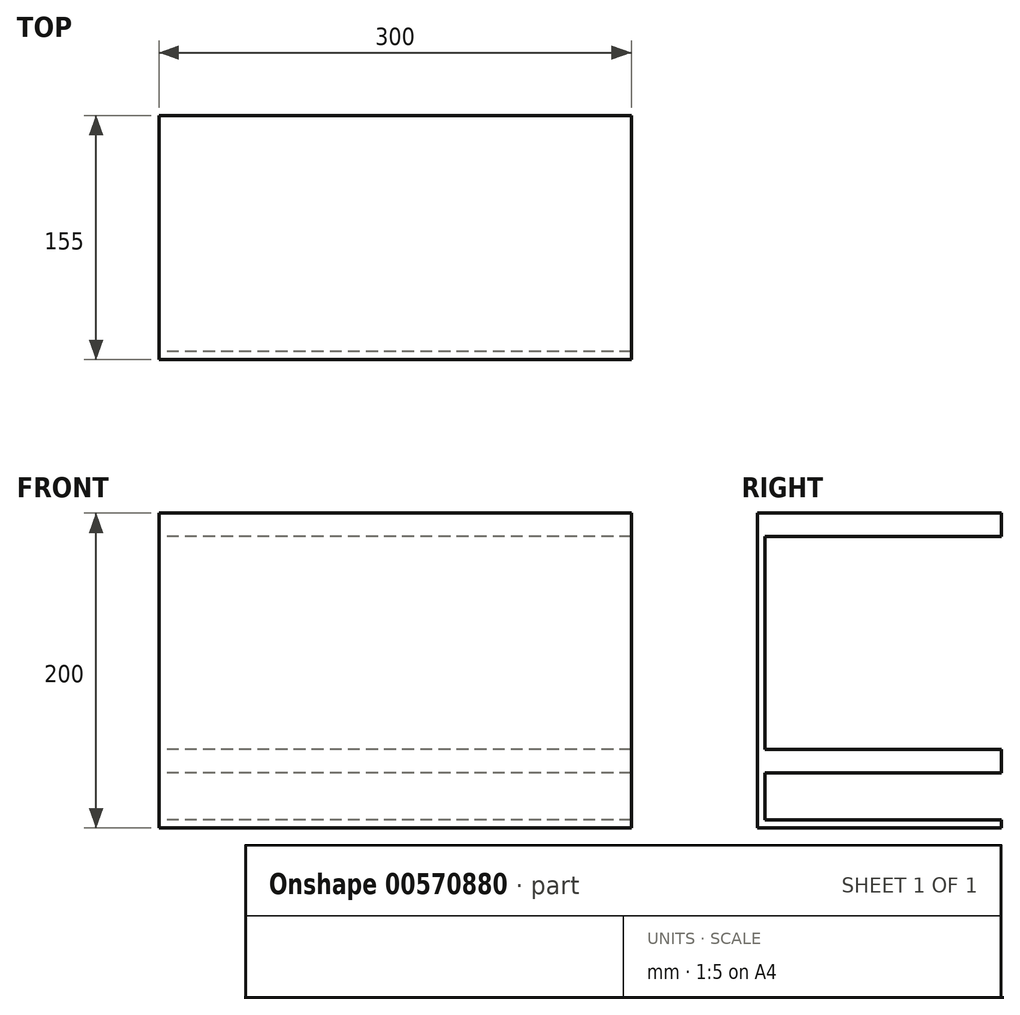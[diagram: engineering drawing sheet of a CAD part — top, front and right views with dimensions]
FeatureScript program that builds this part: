
annotation { "Feature Type Name" : "Feature", "Feature Type Description" : "" }
export const myFeature = defineFeature(function(context is Context, id is Id, definition is map)
    precondition{}
    {
        {
            var Q0;
            Q0=qCreatedBy(makeId("Front.planeOp"),FACE);
            var sketch = newSketch(context, id + "F0", { "sketchPlane" : qUnion([Q0])});
            skLineSegment(sketch, "E0.bottom", {"start": v(150, -100) * mm, "end": v(-150, -100) * mm});
            skLineSegment(sketch, "E0.top", {"start": v(150, 100) * mm, "end": v(-150, 100) * mm});
            skLineSegment(sketch, "E0.left", {"start": v(150, -100) * mm, "end": v(150, 100) * mm});
            skLineSegment(sketch, "E0.right", {"start": v(-150, -100) * mm, "end": v(-150, 100) * mm});
            skPoint(sketch, "E0.middle", {"position": v(0, 0) * mm});
            skSolve(sketch);
        }
        {
            var Q0;
            Q0=makeQuery(id+"F0.imprint","IMPRINT",FACE,{"disambiguationData":[TD([[makeQuery(id+"F0.imprint","IMPRINT",EDGE,{"derivedFrom":sQuery(id+"F0.wireOp",EDGE,"E0.bottom")}),-1.0]])]});
            extrude(context, id + "F1", {"entities" : qUnion([Q0]), "depth" : 5 * mm, "offsetDistance" : 25.4 * mm});
        }
        {
            var Q0;
            Q0=makeQuery(id+"F1.opExtrude","CAP_FACE",FACE,{"disambiguationData":[OSD([sQuery(id+"F0.wireOp",EDGE,"E0.bottom"),sQuery(id+"F0.wireOp",EDGE,"E0.top"),sQuery(id+"F0.wireOp",EDGE,"E0.left"),sQuery(id+"F0.wireOp",EDGE,"E0.right")])],"isStart":true});
            var sketch = newSketch(context, id + "F2", { "sketchPlane" : qUnion([Q0])});
            skLineSegment(sketch, "E1.bottom", {"start": v(-150, 100) * mm, "end": v(150, 100) * mm});
            skLineSegment(sketch, "E1.top", {"start": v(-150, 85) * mm, "end": v(150, 85) * mm});
            skLineSegment(sketch, "E1.left", {"start": v(-150, 100) * mm, "end": v(-150, 85) * mm});
            skLineSegment(sketch, "E1.right", {"start": v(150, 100) * mm, "end": v(150, 85) * mm});
            skLineSegment(sketch, "E2.bottom", {"start": v(-150, -100) * mm, "end": v(150, -100) * mm});
            skLineSegment(sketch, "E2.top", {"start": v(-150, -95) * mm, "end": v(150, -95) * mm});
            skLineSegment(sketch, "E2.left", {"start": v(-150, -100) * mm, "end": v(-150, -95) * mm});
            skLineSegment(sketch, "E2.right", {"start": v(150, -100) * mm, "end": v(150, -95) * mm});
            skLineSegment(sketch, "E3.bottom", {"start": v(-150, -65) * mm, "end": v(150, -65) * mm});
            skLineSegment(sketch, "E3.top", {"start": v(-150, -50) * mm, "end": v(150, -50) * mm});
            skLineSegment(sketch, "E3.left", {"start": v(-150, -65) * mm, "end": v(-150, -50) * mm});
            skLineSegment(sketch, "E3.right", {"start": v(150, -65) * mm, "end": v(150, -50) * mm});
            skSolve(sketch);
        }
        {
            var Q0;
            Q0=makeQuery(id+"F2.imprint","IMPRINT",FACE,{"disambiguationData":[TD([[makeQuery(id+"F2.imprint","IMPRINT",EDGE,{"derivedFrom":sQuery(id+"F2.wireOp",EDGE,"E1.bottom")}),-1.0]])]});
            var Q1;
            Q1=makeQuery(id+"F2.imprint","IMPRINT",FACE,{"disambiguationData":[TD([[makeQuery(id+"F2.imprint","IMPRINT",EDGE,{"derivedFrom":sQuery(id+"F2.wireOp",EDGE,"E3.bottom")}),1.0]])]});
            var Q2;
            Q2=makeQuery(id+"F2.imprint","IMPRINT",FACE,{"disambiguationData":[TD([[makeQuery(id+"F2.imprint","IMPRINT",EDGE,{"derivedFrom":sQuery(id+"F2.wireOp",EDGE,"E2.bottom")}),1.0]])]});
            extrude(context, id + "F3", {"entities" : qUnion([Q0, Q1, Q2]), "operationType" : NewBodyOperationType.ADD, "depth" : 150 * mm, "offsetDistance" : 25.4 * mm});
        }
    });
